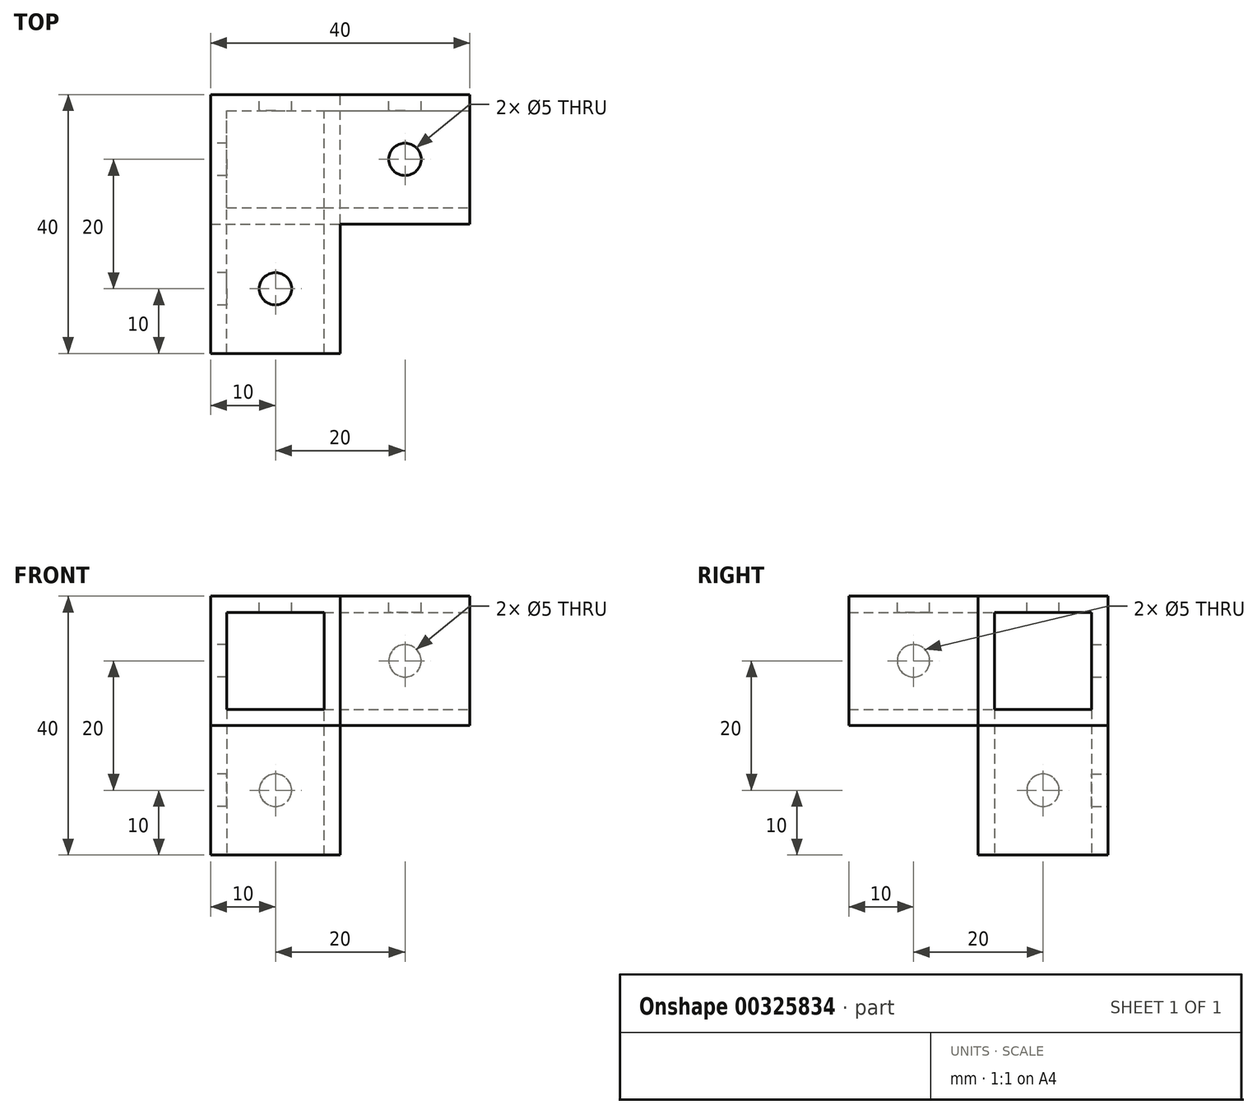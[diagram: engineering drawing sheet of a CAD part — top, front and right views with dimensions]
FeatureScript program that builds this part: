
annotation { "Feature Type Name" : "Feature", "Feature Type Description" : "" }
export const myFeature = defineFeature(function(context is Context, id is Id, definition is map)
    precondition{}
    {
        {
            var Q0;
            Q0=qCreatedBy(makeId("Front.planeOp"),FACE);
            var sketch = newSketch(context, id + "F0", { "sketchPlane" : qUnion([Q0])});
            skLineSegment(sketch, "E0", {"start": v(0, 0) * mm, "end": v(40, 0) * mm});
            skLineSegment(sketch, "E1", {"start": v(0, 0) * mm, "end": v(0, -40) * mm});
            skLineSegment(sketch, "E2", {"start": v(0, -40) * mm, "end": v(20, -40) * mm});
            skLineSegment(sketch, "E3", {"start": v(20, -40) * mm, "end": v(20, -20) * mm});
            skLineSegment(sketch, "E4", {"start": v(20, -20) * mm, "end": v(40, -20) * mm});
            skLineSegment(sketch, "E5", {"start": v(40, 0) * mm, "end": v(40, -20) * mm});
            skSolve(sketch);
        }
        {
            var Q0;
            Q0 = qSketchRegion(id + "F0", true);
            extrude(context, id + "F1", {"entities" : qUnion([Q0]), "depth" : 20 * mm});
        }
        {
            var Q0;
            Q0=makeQuery(id+"F1.opExtrude","CAP_FACE",FACE,{"disambiguationData":[OSD([sQuery(id+"F0.wireOp",EDGE,"E0"),sQuery(id+"F0.wireOp",EDGE,"E1"),sQuery(id+"F0.wireOp",EDGE,"E2"),sQuery(id+"F0.wireOp",EDGE,"E3"),sQuery(id+"F0.wireOp",EDGE,"E4"),sQuery(id+"F0.wireOp",EDGE,"E5")])],"isStart":false});
            var sketch = newSketch(context, id + "F2", { "sketchPlane" : qUnion([Q0])});
            skLineSegment(sketch, "E6.bottom", {"start": v(0, 0) * mm, "end": v(20, 0) * mm});
            skLineSegment(sketch, "E6.top", {"start": v(0, -20) * mm, "end": v(20, -20) * mm});
            skLineSegment(sketch, "E6.left", {"start": v(0, 0) * mm, "end": v(0, -20) * mm});
            skLineSegment(sketch, "E6.right", {"start": v(20, 0) * mm, "end": v(20, -20) * mm});
            skSolve(sketch);
        }
        {
            var Q0;
            Q0 = qSketchRegion(id + "F2", true);
            extrude(context, id + "F3", {"entities" : qUnion([Q0]), "operationType" : NewBodyOperationType.ADD, "depth" : 20 * mm});
        }
        {
            var Q0;
            Q0=makeQuery(id+"F3.opExtrude","CAP_FACE",FACE,{"disambiguationData":[OSD([sQuery(id+"F2.wireOp",EDGE,"E6.bottom"),sQuery(id+"F2.wireOp",EDGE,"E6.top"),sQuery(id+"F2.wireOp",EDGE,"E6.left"),sQuery(id+"F2.wireOp",EDGE,"E6.right")])],"isStart":false});
            var Q1;
            Q1=makeQuery(id+"F1.opExtrude","SWEPT_FACE",FACE,{"disambiguationData":[OSD([sQuery(id+"F0.wireOp",EDGE,"E5")])]});
            var Q2;
            Q2=makeQuery(id+"F1.opExtrude","SWEPT_FACE",FACE,{"disambiguationData":[OSD([sQuery(id+"F0.wireOp",EDGE,"E2")])]});
            shell(context, id + "F4", {"entities" : qUnion([Q0, Q1, Q2]), "thickness" : 2.5 * mm});
        }
        {
            var Q0;
            Q0=makeQuery(id+"F3.boolean.opBoolean","MERGE",FACE,{"derivedFrom":[makeQuery(id+"F1.opExtrude","SWEPT_FACE",FACE,{"disambiguationData":[OSD([sQuery(id+"F0.wireOp",EDGE,"E1")])]}),makeQuery(id+"F3.opExtrude","SWEPT_FACE",FACE,{"disambiguationData":[OSD([sQuery(id+"F2.wireOp",EDGE,"E6.left")])]})]});
            var sketch = newSketch(context, id + "F5", { "sketchPlane" : qUnion([Q0])});
            skCircle(sketch, "E7", {"center": v(30, -10) * mm, "radius": 2.5 * mm});
            skLineSegment(sketch, "E8", {"start": v(40, -20) * mm, "end": v(20, -20) * mm, "construction": true});
            skLineSegment(sketch, "E9", {"start": v(20, -20) * mm, "end": v(20, 0) * mm, "construction": true});
            skLineSegment(sketch, "E10", {"start": v(20, 0) * mm, "end": v(40, 0) * mm, "construction": true});
            skLineSegment(sketch, "E11", {"start": v(20, 0) * mm, "end": v(40, -20) * mm, "construction": true});
            skLineSegment(sketch, "E12", {"start": v(40, 0) * mm, "end": v(20, -20) * mm, "construction": true});
            skLineSegment(sketch, "E13", {"start": v(20, -20) * mm, "end": v(0, -20) * mm, "construction": true});
            skLineSegment(sketch, "E14", {"start": v(0, -20) * mm, "end": v(20, -40) * mm, "construction": true});
            skLineSegment(sketch, "E15", {"start": v(20, -40) * mm, "end": v(20, -20) * mm, "construction": true});
            skLineSegment(sketch, "E16", {"start": v(20, -20) * mm, "end": v(0, -40) * mm, "construction": true});
            skLineSegment(sketch, "E17", {"start": v(0, -40) * mm, "end": v(0, -20) * mm, "construction": true});
            skLineSegment(sketch, "E18", {"start": v(0, -40) * mm, "end": v(20, -40) * mm, "construction": true});
            skCircle(sketch, "E19", {"center": v(10, -30) * mm, "radius": 2.5 * mm});
            skPoint(sketch, "E19.centerSnap0", {"position": v(10, -30) * mm});
            skSolve(sketch);
        }
        {
            var Q0;
            Q0 = qSketchRegion(id + "F5", true);
            extrude(context, id + "F6", {"entities" : qUnion([Q0]), "operationType" : NewBodyOperationType.REMOVE, "endBound" : BoundingType.UP_TO_NEXT, "oppositeDirection" : true, "depth" : 25 * mm});
        }
        {
            var Q0;
            Q0=makeQuery(id+"F3.boolean.opBoolean","MERGE",FACE,{"derivedFrom":[makeQuery(id+"F1.opExtrude","SWEPT_FACE",FACE,{"disambiguationData":[OSD([sQuery(id+"F0.wireOp",EDGE,"E0")])]}),makeQuery(id+"F3.opExtrude","SWEPT_FACE",FACE,{"disambiguationData":[OSD([sQuery(id+"F2.wireOp",EDGE,"E6.bottom")])]})]});
            var sketch = newSketch(context, id + "F7", { "sketchPlane" : qUnion([Q0])});
            skLineSegment(sketch, "E20", {"start": v(20, -40) * mm, "end": v(20, -20) * mm, "construction": true});
            skLineSegment(sketch, "E21", {"start": v(20, -20) * mm, "end": v(0, -20) * mm, "construction": true});
            skLineSegment(sketch, "E22", {"start": v(0, -20) * mm, "end": v(0, -40) * mm, "construction": true});
            skLineSegment(sketch, "E23", {"start": v(0, -40) * mm, "end": v(20, -40) * mm, "construction": true});
            skLineSegment(sketch, "E24", {"start": v(0, -20) * mm, "end": v(20, -40) * mm, "construction": true});
            skLineSegment(sketch, "E25", {"start": v(20, -20) * mm, "end": v(0, -40) * mm, "construction": true});
            skCircle(sketch, "E26", {"center": v(10, -30) * mm, "radius": 2.5 * mm});
            skLineSegment(sketch, "E27", {"start": v(20, -20) * mm, "end": v(20, 0) * mm, "construction": true});
            skLineSegment(sketch, "E28", {"start": v(20, 0) * mm, "end": v(40, 0) * mm, "construction": true});
            skLineSegment(sketch, "E29", {"start": v(40, 0) * mm, "end": v(40, -20) * mm, "construction": true});
            skLineSegment(sketch, "E30", {"start": v(40, -20) * mm, "end": v(20, -20) * mm, "construction": true});
            skLineSegment(sketch, "E31", {"start": v(20, 0) * mm, "end": v(40, -20) * mm, "construction": true});
            skLineSegment(sketch, "E32", {"start": v(40, 0) * mm, "end": v(20, -20) * mm, "construction": true});
            skCircle(sketch, "E33", {"center": v(30, -10) * mm, "radius": 2.5 * mm});
            skPoint(sketch, "E33.centerSnap0", {"position": v(30, -20) * mm});
            skSolve(sketch);
        }
        {
            var Q0;
            Q0 = qSketchRegion(id + "F7", true);
            extrude(context, id + "F8", {"entities" : qUnion([Q0]), "operationType" : NewBodyOperationType.REMOVE, "endBound" : BoundingType.UP_TO_NEXT, "oppositeDirection" : true, "depth" : 25 * mm});
        }
        {
            var Q0;
            Q0=makeQuery(id+"F1.opExtrude","CAP_FACE",FACE,{"disambiguationData":[OSD([sQuery(id+"F0.wireOp",EDGE,"E0"),sQuery(id+"F0.wireOp",EDGE,"E1"),sQuery(id+"F0.wireOp",EDGE,"E2"),sQuery(id+"F0.wireOp",EDGE,"E3"),sQuery(id+"F0.wireOp",EDGE,"E4"),sQuery(id+"F0.wireOp",EDGE,"E5")])],"isStart":true});
            var sketch = newSketch(context, id + "F9", { "sketchPlane" : qUnion([Q0])});
            skLineSegment(sketch, "E34", {"start": v(-40, 0) * mm, "end": v(-20, -20) * mm, "construction": true});
            skLineSegment(sketch, "E35", {"start": v(-20, -20) * mm, "end": v(-40, -20) * mm, "construction": true});
            skLineSegment(sketch, "E36", {"start": v(-40, -20) * mm, "end": v(-40, 0) * mm, "construction": true});
            skLineSegment(sketch, "E37", {"start": v(-20, -20) * mm, "end": v(-20, 0) * mm, "construction": true});
            skLineSegment(sketch, "E38", {"start": v(-20, 0) * mm, "end": v(-40, -20) * mm, "construction": true});
            skLineSegment(sketch, "E39", {"start": v(-40, 0) * mm, "end": v(-20, 0) * mm, "construction": true});
            skCircle(sketch, "E40", {"center": v(-30, -10) * mm, "radius": 2.5 * mm});
            skLineSegment(sketch, "E41", {"start": v(-20, -20) * mm, "end": v(0, -40) * mm, "construction": true});
            skLineSegment(sketch, "E42", {"start": v(0, -40) * mm, "end": v(-20, -40) * mm, "construction": true});
            skLineSegment(sketch, "E43", {"start": v(-20, -40) * mm, "end": v(-20, -20) * mm, "construction": true});
            skLineSegment(sketch, "E44", {"start": v(-20, -20) * mm, "end": v(0, -20) * mm, "construction": true});
            skLineSegment(sketch, "E45", {"start": v(0, -20) * mm, "end": v(0, -40) * mm, "construction": true});
            skLineSegment(sketch, "E46", {"start": v(0, -20) * mm, "end": v(-20, -40) * mm, "construction": true});
            skCircle(sketch, "E47", {"center": v(-10, -30) * mm, "radius": 2.5 * mm});
            skSolve(sketch);
        }
        {
            var Q0;
            Q0 = qSketchRegion(id + "F9", true);
            extrude(context, id + "F10", {"entities" : qUnion([Q0]), "operationType" : NewBodyOperationType.REMOVE, "endBound" : BoundingType.UP_TO_NEXT, "oppositeDirection" : true, "depth" : 25 * mm});
        }
    });
